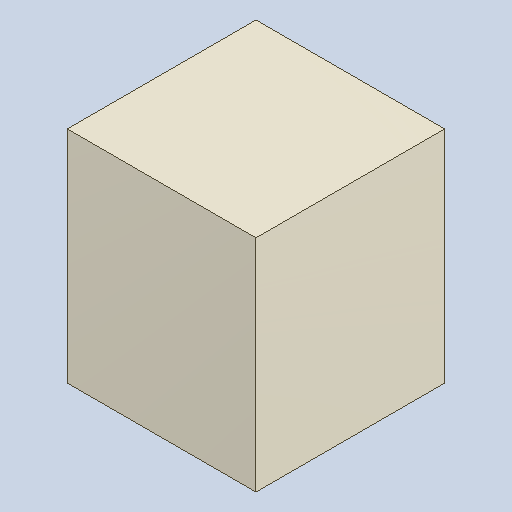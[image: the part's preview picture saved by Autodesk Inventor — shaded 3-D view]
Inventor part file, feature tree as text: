
AUTODESK INVENTOR PART (.ipt)
format: ipt  version: 2023.4 (Build 274418000, 418)  size: 82,944 bytes
history: native  units: mm
features: extrude x1
ambient origin geometry x8: Origin, YZ Plane, XZ Plane, XY Plane, X Axis, Y Axis, Z Axis, Center Point
bodies: Solid1 (feature_tree)
feature tree (1):
  extrude  "Extruded_31"  [1 undecoded]
note: 1 required parameter value undecoded (feature->parameter linkage not recoverable at this tier; creation-order binding heuristic only, values carry confidence <= 0.55)
